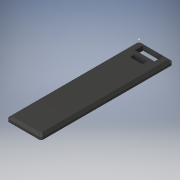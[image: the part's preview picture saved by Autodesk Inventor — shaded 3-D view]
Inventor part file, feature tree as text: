
AUTODESK INVENTOR PART (.ipt)
format: ipt  version: 2019 (Build 230136000, 136)  size: 158,208 bytes
history: native  units: mm
features: sketch x4, extrude x3, chamfer x3
ambient origin geometry x8: Origin, YZ Plane, XZ Plane, XY Plane, X Axis, Y Axis, Z Axis, Center Point
bodies: Solid1 (feature_tree)
feature tree (10):
  extrude  "Extrusion1"  Depth=3.0mm
  extrude  "Extrusion2"  Depth=2.0mm
  extrude  "Extrusion3"  Depth=6.5mm
  sketch  "Sketch4"  dims[d7=5.5mm d8=6.5mm d9=5.5mm d10=3.0mm d11=0.0mm d12=2.5mm d13=90.0deg d14=4.0mm d15=3.0mm d16=4.0mm d17=3.0mm d18=3.0mm d19=0.0mm d20=1.5mm d21=2.0mm d22=45.0deg d23=1.0mm d24=2.0mm d25=45.0deg d26=0.8165mm d27=2.0mm d28=45.0deg]
  chamfer  "Chamfer1"  Distance=6.5mm
  chamfer  "Chamfer2"  Distance=5.5mm
  chamfer  "Chamfer3"  Distance=3.0mm
  sketch  "Sketch1"  dims[d0=22.5mm d1=3.0mm]
  sketch  "Sketch2"  dims[d2=86.75mm d3=0.0mm d4=2.0mm]
  sketch  "Sketch3"  dims[d5=90.0deg d6=6.5mm]
